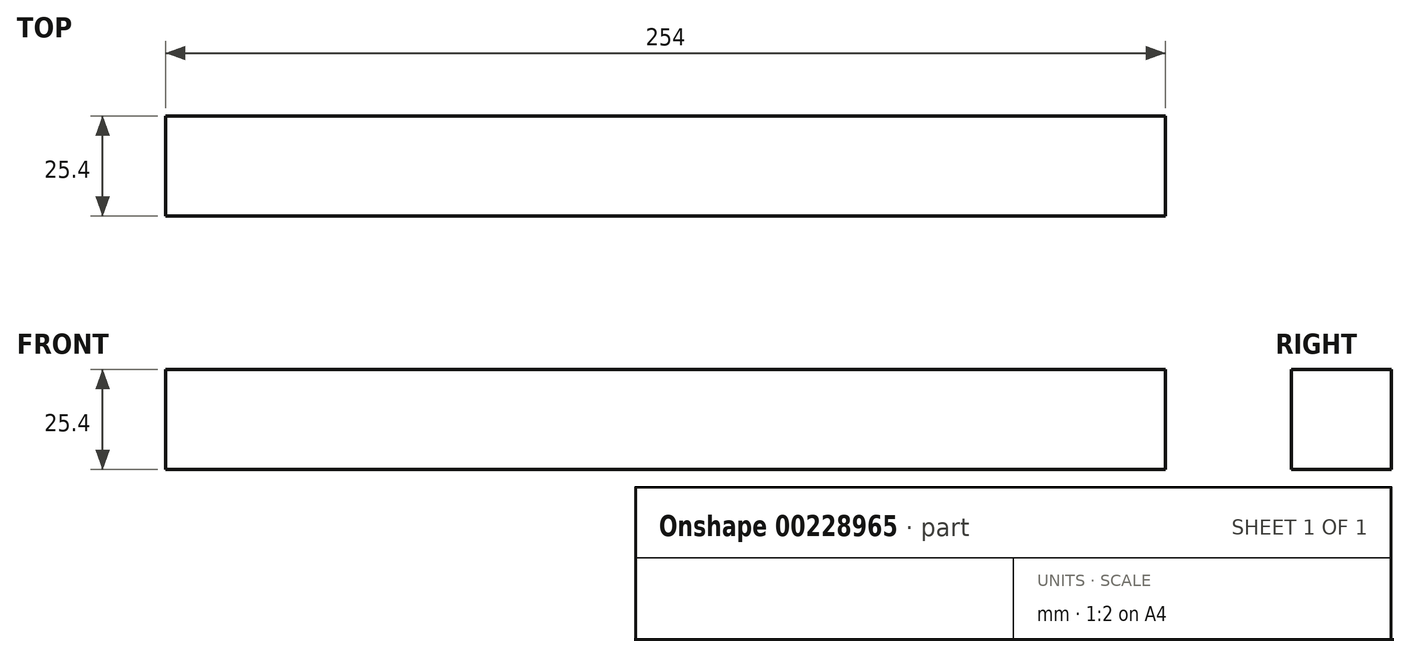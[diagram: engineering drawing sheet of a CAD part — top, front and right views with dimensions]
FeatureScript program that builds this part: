
annotation { "Feature Type Name" : "Feature", "Feature Type Description" : "" }
export const myFeature = defineFeature(function(context is Context, id is Id, definition is map)
    precondition{}
    {
        {
            var Q0;
            Q0=qCreatedBy(makeId("Top.planeOp"),FACE);
            var sketch = newSketch(context, id + "F0", { "sketchPlane" : qUnion([Q0])});
            skLineSegment(sketch, "E0.bottom", {"start": v(0, 0) * mm, "end": v(254, 0) * mm});
            skLineSegment(sketch, "E0.top", {"start": v(0, 25.4) * mm, "end": v(254, 25.4) * mm});
            skLineSegment(sketch, "E0.left", {"start": v(0, 0) * mm, "end": v(0, 25.4) * mm});
            skLineSegment(sketch, "E0.right", {"start": v(254, 0) * mm, "end": v(254, 25.4) * mm});
            skSolve(sketch);
        }
        {
            var Q0;
            Q0 = qSketchRegion(id + "F0", true);
            extrude(context, id + "F1", {"entities" : qUnion([Q0]), "depth" : 25.4 * mm});
        }
    });
